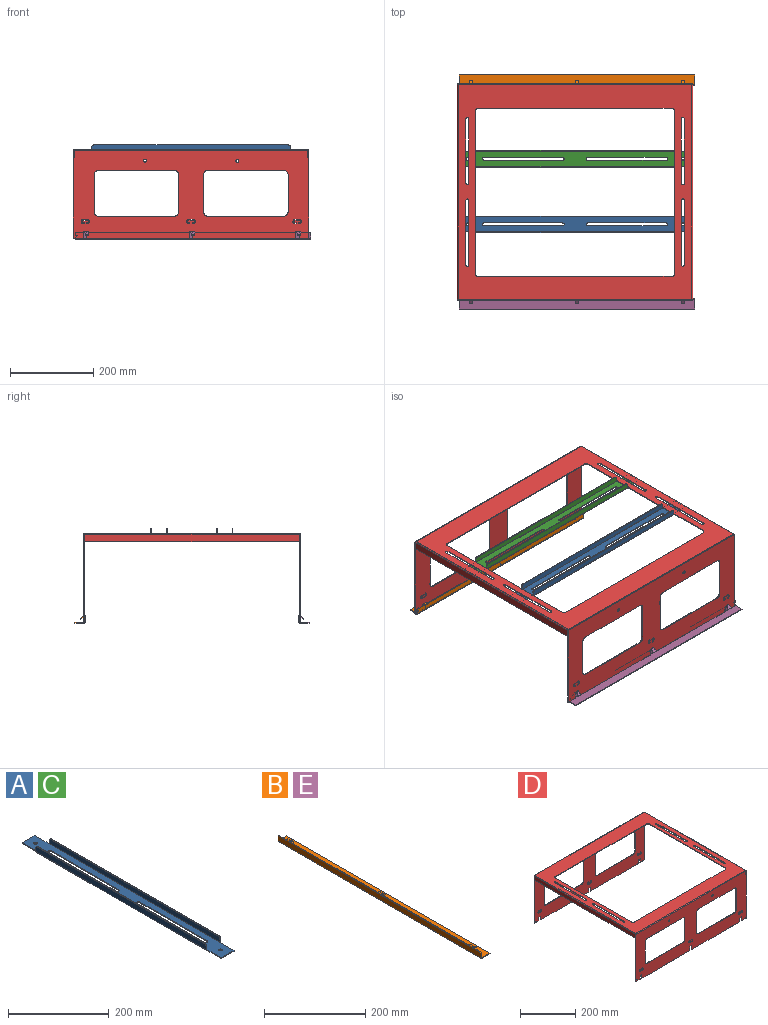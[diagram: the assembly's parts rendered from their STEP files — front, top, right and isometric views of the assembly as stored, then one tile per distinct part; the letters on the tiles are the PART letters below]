
ASSEMBLY  parts=5 mates=6
PART A: 40 faces, bbox 40x558x15 mm
  f0: plane 40x2mm, normal (-1,0,0), area 80mm2, adj f4,f16,f17,f36
  f1: plane 40x2mm, normal (1,0,0), area 80mm2, adj f2,f16,f17,f25
  f2: plane 35.8x2mm, normal (0,1,0), area 71.6mm2, adj f1,f15,f16,f17
  f3: plane 40x2mm, normal (1,0,0), area 80mm2, adj f4,f16,f17,f26
  f4: plane 35.8x2mm, normal (0,-1,0), area 71.6mm2, adj f0,f3,f16,f17
  f5: plane 188.9x2mm, normal (-1,0,0), area 377.8mm2, adj f6,f14,f16,f17
  f6: cylinder r=3.5mm len=7mm, axis (0,0,1), area 22.5mm2, adj f5,f7,f16,f17
  f7: plane 188.85x2mm, normal (1,0,0), area 377.7mm2, adj f6,f14,f16,f17
  f8: cylinder r=3.5mm len=7mm, axis (0,0,1), area 22mm2, adj f9,f11,f16,f17
  f9: plane 188.85x2mm, normal (1,0,0), area 377.7mm2, adj f8,f10,f16,f17
  f10: cylinder r=3.5mm len=7mm, axis (0,0,1), area 22.5mm2, adj f9,f11,f16,f17
  f11: plane 188.9x2mm, normal (-1,0,0), area 377.8mm2, adj f8,f10,f16,f17
  f12: cylinder r=3.5mm len=7mm, axis (0,0,1), area 44mm2, adj f16,f17
  f13: cylinder r=3.5mm len=7mm, axis (0,0,1), area 44mm2, adj f16,f17
  f14: cylinder r=3.5mm len=7mm, axis (0,0,1), area 22mm2, adj f5,f7,f16,f17
  f15: plane 40x2mm, normal (-1,0,0), area 80mm2, adj f2,f16,f17,f37
  f16: plane 558x35.8mm, normal (0,0,-1), area 17177.3mm2, adj f0,f1,f2,f3,f4,f5,f6,f7
  f17: plane 558x35.8mm, normal (0,0,1), area 17177.3mm2, adj f0,f1,f2,f3,f4,f5,f6,f7
  f18: plane 7.9x2mm, normal (0,-1,0), area 15.8mm2, adj f22,f23,f24,f26
  f19: plane 7.9x2mm, normal (0,1,0), area 15.8mm2, adj f20,f23,f24,f25
  f20: cylinder r=5mm len=5mm, axis (1,0,0), area 15.7mm2, adj f19,f21,f23,f24
  f21: plane 468x2mm, normal (0,0,1), area 936mm2, adj f20,f22,f23,f24
  f22: cylinder r=5mm len=5mm, axis (1,0,0), area 15.7mm2, adj f18,f21,f23,f24
  f23: plane 478x12.9mm, normal (1,0,0), area 6155.5mm2, adj f18,f19,f20,f21,f22,f27
  f24: plane 478x12.9mm, normal (-1,0,0), area 6155.5mm2, adj f18,f19,f20,f21,f22,f28
  f25: plane 2.1x2.1mm, normal (0,1,0), area 3.5mm2, adj f1,f19,f27,f28
  f26: plane 2.1x2.1mm, normal (0,-1,0), area 3.5mm2, adj f3,f18,f27,f28
  f27: cylinder r=2.1mm len=478mm, axis (0,1,0), area 1576.8mm2, adj f16,f23,f25,f26
  f28: cylinder r=0.1mm len=478mm, axis (0,1,0), area 75.1mm2, adj f17,f24,f25,f26
  f29: plane 468x2mm, normal (0,0,1), area 936mm2, adj f30,f33,f34,f35
  f30: cylinder r=5mm len=5mm, axis (-1,0,0), area 15.7mm2, adj f29,f31,f34,f35
  f31: plane 7.9x2mm, normal (0,1,0), area 15.8mm2, adj f30,f34,f35,f37
  f32: plane 7.9x2mm, normal (0,-1,0), area 15.8mm2, adj f33,f34,f35,f36
  f33: cylinder r=5mm len=5mm, axis (-1,0,0), area 15.7mm2, adj f29,f32,f34,f35
  f34: plane 478x12.9mm, normal (-1,0,0), area 6155.5mm2, adj f29,f30,f31,f32,f33,f38
  f35: plane 478x12.9mm, normal (1,0,0), area 6155.5mm2, adj f29,f30,f31,f32,f33,f39
  f36: plane 2.1x2.1mm, normal (0,-1,0), area 3.5mm2, adj f0,f32,f38,f39
  f37: plane 2.1x2.1mm, normal (0,1,0), area 3.5mm2, adj f15,f31,f38,f39
  f38: cylinder r=2.1mm len=478mm, axis (0,-1,0), area 1576.8mm2, adj f16,f34,f36,f37
  f39: cylinder r=0.1mm len=478mm, axis (0,-1,0), area 75.1mm2, adj f17,f35,f36,f37
PART B: 62 faces, bbox 25x566x17.9 mm
  f0: plane 22.9x2mm, normal (0,-1,0), area 45.8mm2, adj f2,f3,f4,f58
  f1: plane 22.9x2mm, normal (0,1,0), area 45.8mm2, adj f2,f3,f4,f59
  f2: plane 566x2mm, normal (1,0,0), area 1132mm2, adj f0,f1,f3,f4
  f3: plane 566x22.9mm, normal (0,0,-1), area 12961.4mm2, adj f0,f1,f2,f60
  f4: plane 566x22.9mm, normal (0,0,1), area 12961.4mm2, adj f0,f1,f2,f61
  f5: plane 2x0.27mm, normal (0,0,1), area 0.5mm2, adj f15,f16,f18,f30
  f6: plane 22.15x2mm, normal (0,0,1), area 44.3mm2, adj f15,f16,f17,f30
  f7: plane 2x0.27mm, normal (0,0,1), area 0.5mm2, adj f15,f16,f19,f29
  f8: plane 243.29x2mm, normal (0,0,1), area 486.6mm2, adj f15,f16,f28,f29
  f9: plane 2x0.27mm, normal (0,0,1), area 0.5mm2, adj f15,f16,f20,f28
  f10: plane 2x0.27mm, normal (0,0,1), area 0.5mm2, adj f15,f16,f21,f27
  f11: plane 243.29x2mm, normal (0,0,1), area 486.6mm2, adj f15,f16,f26,f27
  f12: plane 2x0.27mm, normal (0,0,1), area 0.5mm2, adj f15,f16,f22,f26
  f13: plane 2x0.27mm, normal (0,0,1), area 0.5mm2, adj f15,f16,f23,f25
  f14: plane 22.15x2mm, normal (0,0,1), area 44.3mm2, adj f15,f16,f24,f25
  f15: plane 566x13.71mm, normal (-1,0,0), area 7318.5mm2, adj f5,f6,f7,f8,f9,f10,f11,f12
  f16: plane 566x13.71mm, normal (1,0,0), area 7318.5mm2, adj f5,f6,f7,f8,f9,f10,f11,f12
  f17: plane 12.9x2mm, normal (0,-1,0), area 25.8mm2, adj f6,f15,f16,f58
  f18: plane 2x0.81mm, normal (0,-1,0), area 1.6mm2, adj f5,f15,f16,f54
  f19: plane 2x0.81mm, normal (0,1,0), area 1.6mm2, adj f7,f15,f16,f55
  f20: plane 2x0.81mm, normal (0,-1,0), area 1.6mm2, adj f9,f15,f16,f37
  f21: plane 2x0.81mm, normal (0,1,0), area 1.6mm2, adj f10,f15,f16,f36
  f22: plane 2x0.81mm, normal (0,-1,0), area 1.6mm2, adj f12,f15,f16,f46
  f23: plane 2x0.81mm, normal (0,1,0), area 1.6mm2, adj f13,f15,f16,f45
  f24: plane 12.9x2mm, normal (0,1,0), area 25.8mm2, adj f14,f15,f16,f59
  f25: cylinder r=1.06mm len=2mm, axis (1,0,0), area 3.6mm2, adj f13,f14,f15,f16
  f26: cylinder r=1.06mm len=2mm, axis (1,0,0), area 3.6mm2, adj f11,f12,f15,f16
  f27: cylinder r=1.06mm len=2mm, axis (1,0,0), area 3.6mm2, adj f10,f11,f15,f16
  f28: cylinder r=1.06mm len=2mm, axis (1,0,0), area 3.6mm2, adj f8,f9,f15,f16
  f29: cylinder r=1.06mm len=2mm, axis (1,0,0), area 3.6mm2, adj f7,f8,f15,f16
  f30: cylinder r=1.06mm len=2mm, axis (1,0,0), area 3.6mm2, adj f5,f6,f15,f16
  f31: plane 8x1.64mm, normal (0.82,0,-0.57), area 16mm2, adj f32,f33,f34,f35
  f32: plane 10.13x7.93mm, normal (0,1,0), area 21.9mm2, adj f31,f34,f35,f36
  f33: plane 10.13x7.93mm, normal (0,-1,0), area 21.9mm2, adj f31,f34,f35,f37
  f34: plane 8.98x8mm, normal (0.57,0,0.82), area 87.7mm2, adj f31,f32,f33,f38
  f35: plane 8.98x8mm, normal (-0.57,0,-0.82), area 87.7mm2, adj f31,f32,f33,f39
  f36: plane 3.3x2.1mm, normal (0,1,0), area 4.8mm2, adj f21,f32,f38,f39
  f37: plane 3.3x2.1mm, normal (0,-1,0), area 4.8mm2, adj f20,f33,f38,f39
  f38: cylinder r=2.1mm len=8mm, axis (0,1,0), area 36.7mm2, adj f15,f34,f36,f37
  f39: cylinder r=0.1mm len=8mm, axis (0,1,0), area 1.7mm2, adj f16,f35,f36,f37
  f40: plane 8x1.64mm, normal (0.82,0,-0.57), area 16mm2, adj f41,f42,f43,f44
  f41: plane 10.13x7.93mm, normal (0,1,0), area 21.9mm2, adj f40,f43,f44,f45
  f42: plane 10.13x7.93mm, normal (0,-1,0), area 21.9mm2, adj f40,f43,f44,f46
  f43: plane 8.98x8mm, normal (0.57,0,0.82), area 87.7mm2, adj f40,f41,f42,f47
  f44: plane 8.98x8mm, normal (-0.57,0,-0.82), area 87.7mm2, adj f40,f41,f42,f48
  f45: plane 3.3x2.1mm, normal (0,1,0), area 4.8mm2, adj f23,f41,f47,f48
  f46: plane 3.3x2.1mm, normal (0,-1,0), area 4.8mm2, adj f22,f42,f47,f48
  f47: cylinder r=2.1mm len=8mm, axis (0,1,0), area 36.7mm2, adj f15,f43,f45,f46
  f48: cylinder r=0.1mm len=8mm, axis (0,1,0), area 1.7mm2, adj f16,f44,f45,f46
  f49: plane 8x1.64mm, normal (0.82,0,-0.57), area 16mm2, adj f50,f51,f52,f53
  f50: plane 10.13x7.93mm, normal (0,1,0), area 21.9mm2, adj f49,f52,f53,f55
  f51: plane 10.13x7.93mm, normal (0,-1,0), area 21.9mm2, adj f49,f52,f53,f54
  f52: plane 8.98x8mm, normal (0.57,0,0.82), area 87.7mm2, adj f49,f50,f51,f56
  f53: plane 8.98x8mm, normal (-0.57,0,-0.82), area 87.7mm2, adj f49,f50,f51,f57
  f54: plane 3.3x2.1mm, normal (0,-1,0), area 4.8mm2, adj f18,f51,f56,f57
  f55: plane 3.3x2.1mm, normal (0,1,0), area 4.8mm2, adj f19,f50,f56,f57
  f56: cylinder r=2.1mm len=8mm, axis (0,-1,0), area 36.7mm2, adj f15,f52,f54,f55
  f57: cylinder r=0.1mm len=8mm, axis (0,-1,0), area 1.7mm2, adj f16,f53,f54,f55
  f58: plane 2.1x2.1mm, normal (0,-1,0), area 3.5mm2, adj f0,f17,f60,f61
  f59: plane 2.1x2.1mm, normal (0,1,0), area 3.5mm2, adj f1,f24,f60,f61
  f60: cylinder r=2.1mm len=566mm, axis (0,-1,0), area 1867mm2, adj f3,f15,f58,f59
  f61: cylinder r=0.1mm len=566mm, axis (0,-1,0), area 88.9mm2, adj f4,f16,f58,f59
PART C: same geometry as A
PART D: 200 faces, bbox 566x521x213 mm
  f0: cylinder r=3.5mm len=7mm, axis (0,0,1), area 22mm2, adj f1,f23,f24,f25
  f1: plane 155x2mm, normal (-1,0,0), area 310mm2, adj f0,f2,f24,f25
  f2: cylinder r=3.5mm len=7mm, axis (0,0,1), area 22mm2, adj f1,f23,f24,f25
  f3: plane 390x2mm, normal (1,0,0), area 780mm2, adj f4,f22,f24,f25
  f4: cylinder r=7mm len=7mm, axis (0,0,1), area 22mm2, adj f3,f5,f24,f25
  f5: plane 466x2mm, normal (0,1,0), area 932mm2, adj f4,f6,f24,f25
  f6: cylinder r=7mm len=7mm, axis (0,0,1), area 22mm2, adj f5,f7,f24,f25
  f7: plane 390x2mm, normal (-1,0,0), area 780mm2, adj f6,f8,f24,f25
  f8: cylinder r=7mm len=7mm, axis (0,0,1), area 22mm2, adj f7,f9,f24,f25
  f9: plane 466x2mm, normal (0,-1,0), area 932mm2, adj f8,f22,f24,f25
  f10: plane 155x2mm, normal (1,0,0), area 310mm2, adj f11,f21,f24,f25
  f11: cylinder r=3.5mm len=7mm, axis (0,0,1), area 22mm2, adj f10,f12,f24,f25
  f12: plane 155x2mm, normal (-1,0,0), area 310mm2, adj f11,f21,f24,f25
  f13: cylinder r=3.5mm len=7mm, axis (0,0,1), area 22mm2, adj f14,f20,f24,f25
  f14: plane 155x2mm, normal (1,0,0), area 310mm2, adj f13,f15,f24,f25
  f15: cylinder r=3.5mm len=7mm, axis (0,0,1), area 22mm2, adj f14,f20,f24,f25
  f16: cylinder r=3.5mm len=7mm, axis (0,0,1), area 22mm2, adj f17,f19,f24,f25
  f17: plane 155x2mm, normal (-1,0,0), area 310mm2, adj f16,f18,f24,f25
  f18: cylinder r=3.5mm len=7mm, axis (0,0,1), area 22mm2, adj f17,f19,f24,f25
  f19: plane 155x2mm, normal (1,0,0), area 310mm2, adj f16,f18,f24,f25
  f20: plane 155x2mm, normal (-1,0,0), area 310mm2, adj f13,f15,f24,f25
  f21: cylinder r=3.5mm len=7mm, axis (0,0,1), area 22mm2, adj f10,f12,f24,f25
  f22: cylinder r=7mm len=7mm, axis (0,0,1), area 22mm2, adj f3,f9,f24,f25
  f23: plane 155x2mm, normal (1,0,0), area 310mm2, adj f0,f2,f24,f25
  f24: plane 561.8x516.8mm, normal (0,0,-1), area 91966.4mm2, adj f0,f1,f2,f3,f4,f5,f6,f7
  f25: plane 561.8x516.8mm, normal (0,0,1), area 91966.4mm2, adj f0,f1,f2,f3,f4,f5,f6,f7
  f26: plane 2.1x2mm, normal (0,0,1), area 4.2mm2, adj f40,f98,f99,f101
  f27: plane 9x2mm, normal (0,0,-1), area 18mm2, adj f28,f97,f98,f99
  f28: plane 17x2mm, normal (1,0,0), area 34mm2, adj f27,f29,f98,f99
  f29: plane 246x2mm, normal (0,0,-1), area 492mm2, adj f28,f30,f98,f99
  f30: plane 17x2mm, normal (-1,0,0), area 34mm2, adj f29,f31,f98,f99
  f31: plane 9x2mm, normal (0,0,-1), area 18mm2, adj f30,f32,f98,f99
  f32: plane 17x2mm, normal (1,0,0), area 34mm2, adj f31,f33,f98,f99
  f33: plane 246x2mm, normal (0,0,-1), area 492mm2, adj f32,f34,f98,f99
  f34: plane 17x2mm, normal (-1,0,0), area 34mm2, adj f33,f35,f98,f99
  f35: plane 9x2mm, normal (0,0,-1), area 18mm2, adj f34,f36,f98,f99
  f36: plane 17x2mm, normal (1,0,0), area 34mm2, adj f35,f37,f98,f99
  f37: plane 23.5x2mm, normal (0,0,-1), area 47mm2, adj f36,f38,f98,f99
  f38: plane 210.9x2mm, normal (-1,0,0), area 421.8mm2, adj f37,f39,f98,f99
  f39: plane 2.1x2mm, normal (0,0,1), area 4.2mm2, adj f38,f98,f99,f100
  f40: plane 210.9x2mm, normal (1,0,0), area 421.8mm2, adj f26,f41,f98,f99
  f41: plane 23.5x2mm, normal (0,0,-1), area 47mm2, adj f40,f97,f98,f99
  f42: plane 183x2mm, normal (0,0,-1), area 366mm2, adj f43,f96,f98,f99
  f43: cylinder r=10mm len=10mm, axis (0,1,0), area 31.4mm2, adj f42,f44,f98,f99
  f44: plane 90x2mm, normal (1,0,0), area 180mm2, adj f43,f45,f98,f99
  f45: cylinder r=10mm len=10mm, axis (0,1,0), area 31.4mm2, adj f44,f46,f98,f99
  f46: plane 183x2mm, normal (0,0,1), area 366mm2, adj f45,f47,f98,f99
  f47: cylinder r=10mm len=10mm, axis (0,1,0), area 31.4mm2, adj f46,f48,f98,f99
  f48: plane 90x2mm, normal (-1,0,0), area 180mm2, adj f47,f96,f98,f99
  f49: cylinder r=10mm len=10mm, axis (0,1,0), area 31.4mm2, adj f50,f95,f98,f99
  f50: plane 183x2mm, normal (0,0,-1), area 366mm2, adj f49,f51,f98,f99
  f51: cylinder r=10mm len=10mm, axis (0,1,0), area 31.4mm2, adj f50,f52,f98,f99
  f52: plane 90x2mm, normal (1,0,0), area 180mm2, adj f51,f53,f98,f99
  f53: cylinder r=10mm len=10mm, axis (0,1,0), area 31.4mm2, adj f52,f54,f98,f99
  f54: plane 183x2mm, normal (0,0,1), area 366mm2, adj f53,f55,f98,f99
  f55: cylinder r=10mm len=10mm, axis (0,1,0), area 31.4mm2, adj f54,f95,f98,f99
  f56: cylinder r=5mm len=10mm, axis (0,1,0), area 31.5mm2, adj f57,f94,f98,f99
  f57: plane 2.5x2mm, normal (0,0,1), area 5mm2, adj f56,f58,f98,f99
  f58: plane 2.5x2mm, normal (-1,0,0), area 5mm2, adj f57,f59,f98,f99
  f59: plane 2.5x2mm, normal (0,0,-1), area 5mm2, adj f58,f60,f98,f99
  f60: cylinder r=2.5mm len=4.93mm, axis (0,1,0), area 14.6mm2, adj f59,f61,f98,f99
  f61: plane 10.55x2mm, normal (-0.01,0,1), area 21.1mm2, adj f60,f62,f98,f99
  f62: cylinder r=2.5mm len=5mm, axis (0,1,0), area 15.7mm2, adj f61,f63,f98,f99
  f63: plane 2.5x2mm, normal (0,0,-1), area 5mm2, adj f62,f64,f98,f99
  f64: plane 2.5x2mm, normal (1,0,0), area 5mm2, adj f63,f65,f98,f99
  f65: plane 2.5x2mm, normal (0,0,1), area 5mm2, adj f64,f66,f98,f99
  f66: cylinder r=5mm len=10mm, axis (0,1,0), area 31.4mm2, adj f65,f94,f98,f99
  f67: plane 9.97x2mm, normal (0,0,-1), area 19.9mm2, adj f68,f93,f98,f99
  f68: cylinder r=5mm len=10mm, axis (0,1,0), area 31.4mm2, adj f67,f69,f98,f99
  f69: plane 2.5x2mm, normal (0,0,1), area 5mm2, adj f68,f70,f98,f99
  f70: plane 2.5x2mm, normal (-1,0,0), area 5mm2, adj f69,f71,f98,f99
  f71: plane 2.5x2mm, normal (0,0,-1), area 5mm2, adj f70,f72,f98,f99
  f72: cylinder r=2.5mm len=5mm, axis (0,1,0), area 15.7mm2, adj f71,f73,f98,f99
  f73: plane 10.55x2mm, normal (0.01,0,1), area 21.1mm2, adj f72,f74,f98,f99
  f74: cylinder r=2.5mm len=4.93mm, axis (0,1,0), area 14.6mm2, adj f73,f75,f98,f99
  f75: plane 2.5x2mm, normal (0,0,-1), area 5mm2, adj f74,f76,f98,f99
  f76: plane 2.5x2mm, normal (1,0,0), area 5mm2, adj f75,f77,f98,f99
  f77: plane 2.5x2mm, normal (0,0,1), area 5mm2, adj f76,f93,f98,f99
  f78: plane 2.5x2mm, normal (0,0,1), area 5mm2, adj f79,f90,f98,f99
  f79: cylinder r=5mm len=10mm, axis (0,1,0), area 31.5mm2, adj f78,f80,f98,f99
  f80: plane 9.97x2mm, normal (0,0,-1), area 19.9mm2, adj f79,f81,f98,f99
  f81: cylinder r=5mm len=10mm, axis (0,1,0), area 31.4mm2, adj f80,f82,f98,f99
  f82: plane 2.5x2mm, normal (0,0,1), area 5mm2, adj f81,f83,f98,f99
  f83: plane 2.5x2mm, normal (-1,0,0), area 5mm2, adj f82,f84,f98,f99
  f84: plane 2.5x2mm, normal (0,0,-1), area 5mm2, adj f83,f85,f98,f99
  f85: cylinder r=2.5mm len=5mm, axis (0,1,0), area 15.7mm2, adj f84,f86,f98,f99
  f86: plane 10.55x2mm, normal (0.01,0,1), area 21.1mm2, adj f85,f87,f98,f99
  f87: cylinder r=2.5mm len=4.93mm, axis (0,1,0), area 14.6mm2, adj f86,f88,f98,f99
  f88: plane 2.5x2mm, normal (0,0,-1), area 5mm2, adj f87,f90,f98,f99
  f89: cylinder r=3.5mm len=7mm, axis (0,1,0), area 44mm2, adj f98,f99
  f90: plane 2.5x2mm, normal (1,0,0), area 5mm2, adj f78,f88,f98,f99
  f91: cylinder r=1mm len=2mm, axis (0,1,0), area 12.6mm2, adj f98,f99
  f92: cylinder r=3.5mm len=7mm, axis (0,1,0), area 44mm2, adj f98,f99
  f93: cylinder r=5mm len=10mm, axis (0,1,0), area 31.5mm2, adj f67,f77,f98,f99
  f94: plane 9.97x2mm, normal (0,0,-1), area 19.9mm2, adj f56,f66,f98,f99
  f95: plane 90x2mm, normal (-1,0,0), area 180mm2, adj f49,f55,f98,f99
  f96: cylinder r=10mm len=10mm, axis (0,1,0), area 31.4mm2, adj f42,f48,f98,f99
  f97: plane 17x2mm, normal (-1,0,0), area 34mm2, adj f27,f41,f98,f99
  f98: plane 566x210.9mm, normal (0,1,0), area 74051.8mm2, adj f26,f27,f28,f29,f30,f31,f32,f33
  f99: plane 566x210.9mm, normal (0,-1,0), area 74051.8mm2, adj f26,f27,f28,f29,f30,f31,f32,f33
  f100: plane 2.1x2.1mm, normal (-1,0,0), area 3.5mm2, adj f39,f102,f103,f197
  f101: plane 2.1x2.1mm, normal (1,0,0), area 3.5mm2, adj f26,f102,f103,f187
  f102: cylinder r=2.1mm len=561.8mm, axis (-1,0,0), area 1853.2mm2, adj f25,f99,f100,f101
  f103: cylinder r=0.1mm len=561.8mm, axis (-1,0,0), area 88.2mm2, adj f24,f98,f100,f101
  f104: plane 2.1x2mm, normal (0,0,1), area 4.2mm2, adj f118,f176,f177,f178
  f105: plane 9x2mm, normal (0,0,-1), area 18mm2, adj f106,f175,f176,f177
  f106: plane 17x2mm, normal (-1,0,0), area 34mm2, adj f105,f107,f176,f177
  f107: plane 246x2mm, normal (0,0,-1), area 492mm2, adj f106,f108,f176,f177
  f108: plane 17x2mm, normal (1,0,0), area 34mm2, adj f107,f109,f176,f177
  f109: plane 9x2mm, normal (0,0,-1), area 18mm2, adj f108,f110,f176,f177
  f110: plane 17x2mm, normal (-1,0,0), area 34mm2, adj f109,f111,f176,f177
  f111: plane 246x2mm, normal (0,0,-1), area 492mm2, adj f110,f112,f176,f177
  f112: plane 17x2mm, normal (1,0,0), area 34mm2, adj f111,f113,f176,f177
  f113: plane 9x2mm, normal (0,0,-1), area 18mm2, adj f112,f114,f176,f177
  f114: plane 17x2mm, normal (-1,0,0), area 34mm2, adj f113,f115,f176,f177
  f115: plane 23.5x2mm, normal (0,0,-1), area 47mm2, adj f114,f116,f176,f177
  f116: plane 210.9x2mm, normal (1,0,0), area 421.8mm2, adj f115,f117,f176,f177
  f117: plane 2.1x2mm, normal (0,0,1), area 4.2mm2, adj f116,f176,f177,f179
  f118: plane 210.9x2mm, normal (-1,0,0), area 421.8mm2, adj f104,f119,f176,f177
  f119: plane 23.5x2mm, normal (0,0,-1), area 47mm2, adj f118,f175,f176,f177
  f120: plane 90x2mm, normal (-1,0,0), area 180mm2, adj f121,f174,f176,f177
  f121: cylinder r=10mm len=10mm, axis (0,-1,0), area 31.4mm2, adj f120,f122,f176,f177
  f122: plane 183x2mm, normal (0,0,1), area 366mm2, adj f121,f123,f176,f177
  f123: cylinder r=10mm len=10mm, axis (0,-1,0), area 31.4mm2, adj f122,f124,f176,f177
  f124: plane 90x2mm, normal (1,0,0), area 180mm2, adj f123,f125,f176,f177
  f125: cylinder r=10mm len=10mm, axis (0,-1,0), area 31.4mm2, adj f124,f126,f176,f177
  f126: plane 183x2mm, normal (0,0,-1), area 366mm2, adj f125,f174,f176,f177
  f127: cylinder r=10mm len=10mm, axis (0,-1,0), area 31.4mm2, adj f128,f173,f176,f177
  f128: plane 183x2mm, normal (0,0,1), area 366mm2, adj f127,f129,f176,f177
  f129: cylinder r=10mm len=10mm, axis (0,-1,0), area 31.4mm2, adj f128,f130,f176,f177
  f130: plane 90x2mm, normal (1,0,0), area 180mm2, adj f129,f131,f176,f177
  f131: cylinder r=10mm len=10mm, axis (0,-1,0), area 31.4mm2, adj f130,f132,f176,f177
  f132: plane 183x2mm, normal (0,0,-1), area 366mm2, adj f131,f133,f176,f177
  f133: cylinder r=10mm len=10mm, axis (0,-1,0), area 31.4mm2, adj f132,f173,f176,f177
  f134: cylinder r=5mm len=10mm, axis (0,-1,0), area 31.4mm2, adj f135,f172,f176,f177
  f135: plane 2.5x2mm, normal (0,0,1), area 5mm2, adj f134,f136,f176,f177
  f136: plane 2.5x2mm, normal (1,0,0), area 5mm2, adj f135,f137,f176,f177
  f137: plane 2.5x2mm, normal (0,0,-1), area 5mm2, adj f136,f138,f176,f177
  f138: cylinder r=2.5mm len=5mm, axis (0,-1,0), area 15.7mm2, adj f137,f139,f176,f177
  f139: plane 10.55x2mm, normal (-0.01,0,1), area 21.1mm2, adj f138,f140,f176,f177
  f140: cylinder r=2.5mm len=4.93mm, axis (0,-1,0), area 14.6mm2, adj f139,f141,f176,f177
  f141: plane 2.5x2mm, normal (0,0,-1), area 5mm2, adj f140,f142,f176,f177
  f142: plane 2.5x2mm, normal (-1,0,0), area 5mm2, adj f141,f143,f176,f177
  f143: plane 2.5x2mm, normal (0,0,1), area 5mm2, adj f142,f144,f176,f177
  f144: cylinder r=5mm len=10mm, axis (0,-1,0), area 31.5mm2, adj f143,f172,f176,f177
  f145: plane 2.5x2mm, normal (0,0,1), area 5mm2, adj f146,f171,f176,f177
  f146: plane 2.5x2mm, normal (1,0,0), area 5mm2, adj f145,f147,f176,f177
  f147: plane 2.5x2mm, normal (0,0,-1), area 5mm2, adj f146,f148,f176,f177
  f148: cylinder r=2.5mm len=4.93mm, axis (0,-1,0), area 14.6mm2, adj f147,f149,f176,f177
  f149: plane 10.55x2mm, normal (0.01,0,1), area 21.1mm2, adj f148,f150,f176,f177
  f150: cylinder r=2.5mm len=5mm, axis (0,-1,0), area 15.7mm2, adj f149,f151,f176,f177
  f151: plane 2.5x2mm, normal (0,0,-1), area 5mm2, adj f150,f152,f176,f177
  f152: plane 2.5x2mm, normal (-1,0,0), area 5mm2, adj f151,f153,f176,f177
  f153: plane 2.5x2mm, normal (0,0,1), area 5mm2, adj f152,f154,f176,f177
  f154: cylinder r=5mm len=10mm, axis (0,-1,0), area 31.4mm2, adj f153,f155,f176,f177
  f155: plane 9.97x2mm, normal (0,0,-1), area 19.9mm2, adj f154,f171,f176,f177
  f156: plane 10.55x2mm, normal (0.01,0,1), area 21.1mm2, adj f157,f168,f176,f177
  f157: cylinder r=2.5mm len=5mm, axis (0,-1,0), area 15.7mm2, adj f156,f158,f176,f177
  f158: plane 2.5x2mm, normal (0,0,-1), area 5mm2, adj f157,f159,f176,f177
  f159: plane 2.5x2mm, normal (-1,0,0), area 5mm2, adj f158,f160,f176,f177
  f160: plane 2.5x2mm, normal (0,0,1), area 5mm2, adj f159,f161,f176,f177
  f161: cylinder r=5mm len=10mm, axis (0,-1,0), area 31.4mm2, adj f160,f162,f176,f177
  f162: plane 9.97x2mm, normal (0,0,-1), area 19.9mm2, adj f161,f163,f176,f177
  f163: cylinder r=5mm len=10mm, axis (0,-1,0), area 31.5mm2, adj f162,f164,f176,f177
  f164: plane 2.5x2mm, normal (0,0,1), area 5mm2, adj f163,f165,f176,f177
  f165: plane 2.5x2mm, normal (1,0,0), area 5mm2, adj f164,f166,f176,f177
  f166: plane 2.5x2mm, normal (0,0,-1), area 5mm2, adj f165,f168,f176,f177
  f167: cylinder r=3.5mm len=7mm, axis (0,-1,0), area 44mm2, adj f176,f177
  f168: cylinder r=2.5mm len=4.93mm, axis (0,-1,0), area 14.6mm2, adj f156,f166,f176,f177
  f169: cylinder r=1mm len=2mm, axis (0,-1,0), area 12.6mm2, adj f176,f177
  f170: cylinder r=3.5mm len=7mm, axis (0,-1,0), area 44mm2, adj f176,f177
  f171: cylinder r=5mm len=10mm, axis (0,-1,0), area 31.5mm2, adj f145,f155,f176,f177
  f172: plane 9.97x2mm, normal (0,0,-1), area 19.9mm2, adj f134,f144,f176,f177
  f173: plane 90x2mm, normal (-1,0,0), area 180mm2, adj f127,f133,f176,f177
  f174: cylinder r=10mm len=10mm, axis (0,-1,0), area 31.4mm2, adj f120,f126,f176,f177
  f175: plane 17x2mm, normal (1,0,0), area 34mm2, adj f105,f119,f176,f177
  f176: plane 566x210.9mm, normal (0,-1,0), area 74051.8mm2, adj f104,f105,f106,f107,f108,f109,f110,f111
  f177: plane 566x210.9mm, normal (0,1,0), area 74051.8mm2, adj f104,f105,f106,f107,f108,f109,f110,f111
  f178: plane 2.1x2.1mm, normal (-1,0,0), area 3.5mm2, adj f104,f180,f181,f196
  f179: plane 2.1x2.1mm, normal (1,0,0), area 3.5mm2, adj f117,f180,f181,f188
  f180: cylinder r=2.1mm len=561.8mm, axis (-1,0,0), area 1853.2mm2, adj f25,f177,f178,f179
  f181: cylinder r=0.1mm len=561.8mm, axis (-1,0,0), area 88.2mm2, adj f24,f176,f178,f179
  f182: plane 516.8x2mm, normal (0,0,-1), area 1033.6mm2, adj f183,f184,f185,f186
  f183: plane 17.9x2mm, normal (0,-1,0), area 35.8mm2, adj f182,f185,f186,f187
  f184: plane 17.9x2mm, normal (0,1,0), area 35.8mm2, adj f182,f185,f186,f188
  f185: plane 516.8x17.9mm, normal (-1,0,0), area 9250.7mm2, adj f182,f183,f184,f190
  f186: plane 516.8x17.9mm, normal (1,0,0), area 9250.7mm2, adj f182,f183,f184,f189
  f187: plane 2.1x2.1mm, normal (0,-1,0), area 3.5mm2, adj f101,f183,f189,f190
  f188: plane 2.1x2.1mm, normal (0,1,0), area 3.5mm2, adj f179,f184,f189,f190
  f189: cylinder r=2.1mm len=516.8mm, axis (0,-1,0), area 1704.8mm2, adj f25,f186,f187,f188
  f190: cylinder r=0.1mm len=516.8mm, axis (0,-1,0), area 81.2mm2, adj f24,f185,f187,f188
  f191: plane 516.8x2mm, normal (0,0,-1), area 1033.6mm2, adj f192,f193,f194,f195
  f192: plane 17.9x2mm, normal (0,1,0), area 35.8mm2, adj f191,f194,f195,f196
  f193: plane 17.9x2mm, normal (0,-1,0), area 35.8mm2, adj f191,f194,f195,f197
  f194: plane 516.8x17.9mm, normal (1,0,0), area 9250.7mm2, adj f191,f192,f193,f199
  f195: plane 516.8x17.9mm, normal (-1,0,0), area 9250.7mm2, adj f191,f192,f193,f198
  f196: plane 2.1x2.1mm, normal (0,1,0), area 3.5mm2, adj f178,f192,f198,f199
  f197: plane 2.1x2.1mm, normal (0,-1,0), area 3.5mm2, adj f100,f193,f198,f199
  f198: cylinder r=2.1mm len=516.8mm, axis (0,1,0), area 1704.8mm2, adj f25,f195,f196,f197
  f199: cylinder r=0.1mm len=516.8mm, axis (0,1,0), area 81.2mm2, adj f24,f194,f196,f197
PART E: same geometry as B
PLACE A rot(axis=(0,0,-1),90deg) t=(2.21,-78.32,66.29)mm
PLACE B rot(axis=(0,0,1),90deg) t=(6.45,268.9,-144.71)mm
PLACE C rot(axis=(0,0,-1),90deg) t=(2.21,79.47,66.29)mm
PLACE D t=(2.21,0,68.29)mm
PLACE E rot(axis=(0,0,-1),90deg) t=(6.45,-268.9,-144.71)mm
MATE parallel C.f12 <-> D.f21  axis (0,0,1) through (-256.79,79.47,68.29)mm
MATE planar E.f4 <-> D.f41  axis (0,0,1) through (289.45,-258.5,-142.71)mm
MATE planar B.f4 <-> D.f115  axis (0,0,1) through (289.45,258.5,-142.71)mm
MATE parallel C.f12 <-> D.f21  axis (0,0,1) through (-256.79,79.47,68.29)mm
MATE pin_slot A.f12 <-> D.f18  axis (0,0,1) through (-256.79,-78.32,68.29)mm
MATE pin_slot C.f12 <-> D.f24  axis (0,0,1) through (-256.79,79.47,68.29)mm
